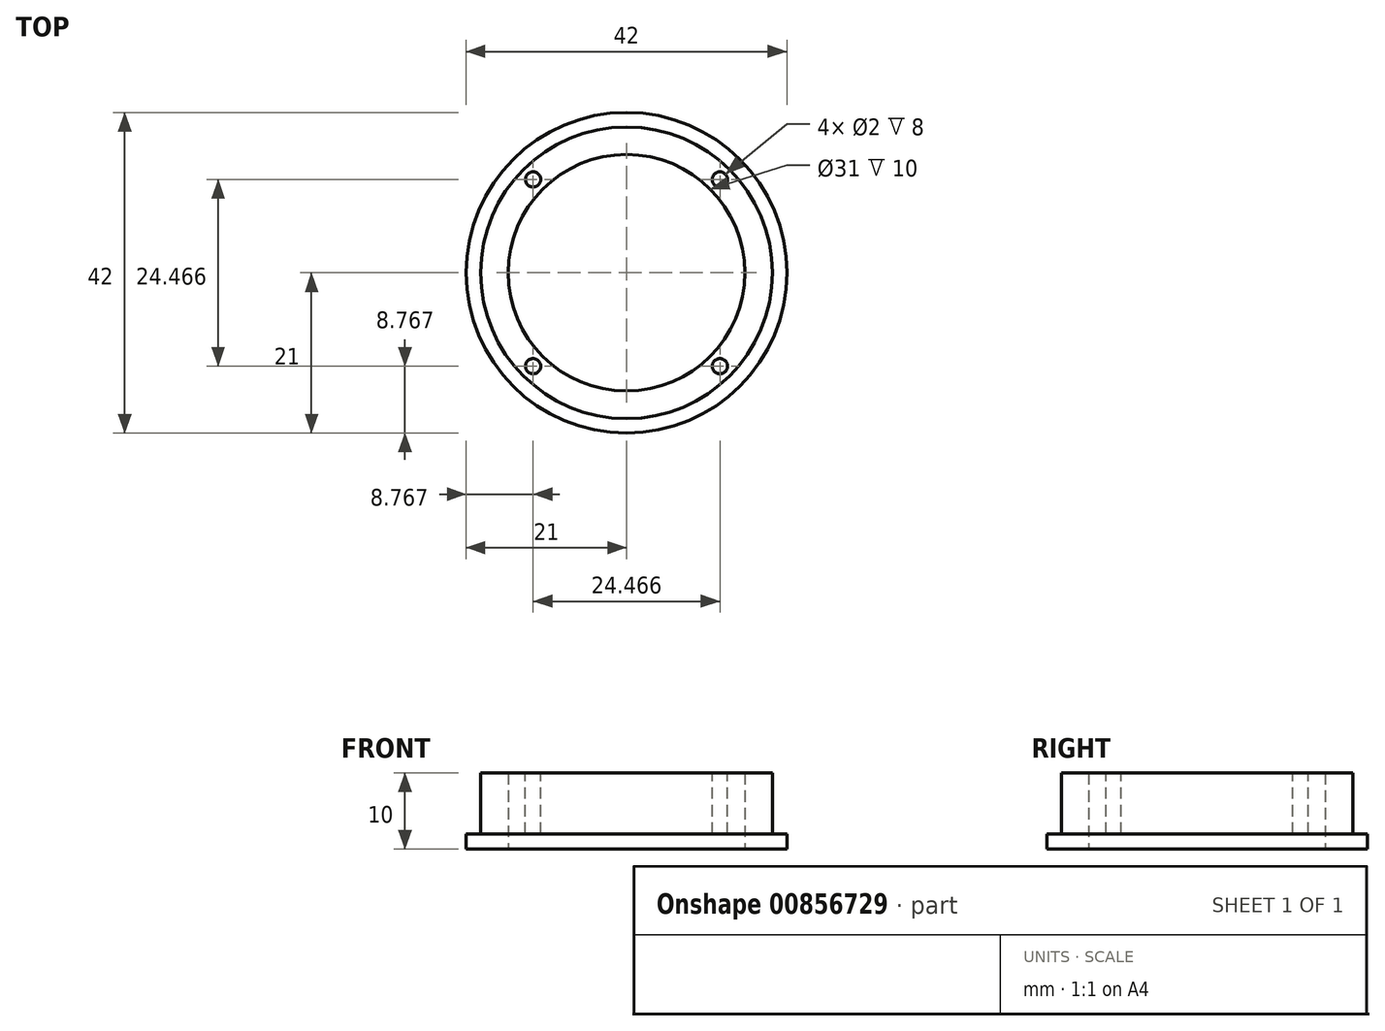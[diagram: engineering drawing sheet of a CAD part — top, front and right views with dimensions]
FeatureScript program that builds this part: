
annotation { "Feature Type Name" : "Feature", "Feature Type Description" : "" }
export const myFeature = defineFeature(function(context is Context, id is Id, definition is map)
    precondition{}
    {
        {
            var Q0;
            Q0=qCreatedBy(makeId("Top.planeOp"),FACE);
            var sketch = newSketch(context, id + "F0", { "sketchPlane" : qUnion([Q0])});
            skCircle(sketch, "E0", {"center": v(0, 0) * mm, "radius": 21 * mm});
            skSolve(sketch);
        }
        {
            var Q0;
            Q0=makeQuery(id+"F0.imprint","IMPRINT",FACE,{"disambiguationData":[TD([[makeQuery(id+"F0.imprint","IMPRINT",EDGE,{"derivedFrom":sQuery(id+"F0.wireOp",EDGE,"E0")}),1.0]])]});
            extrude(context, id + "F1", {"entities" : qUnion([Q0]), "depth" : 2 * mm, "offsetDistance" : 25 * mm});
        }
        {
            var Q0;
            Q0=makeQuery(id+"F1.opExtrude","CAP_FACE",FACE,{"disambiguationData":[OSD([sQuery(id+"F0.wireOp",EDGE,"E0")])],"isStart":false});
            var sketch = newSketch(context, id + "F2", { "sketchPlane" : qUnion([Q0])});
            skCircle(sketch, "E1", {"center": v(0, 0) * mm, "radius": 19.1 * mm});
            skSolve(sketch);
        }
        {
            var Q0;
            Q0=makeQuery(id+"F2.imprint","IMPRINT",FACE,{"disambiguationData":[TD([[makeQuery(id+"F2.imprint","IMPRINT",EDGE,{"derivedFrom":sQuery(id+"F2.wireOp",EDGE,"E1")}),1.0]])]});
            extrude(context, id + "F3", {"entities" : qUnion([Q0]), "operationType" : NewBodyOperationType.ADD, "depth" : 8 * mm, "offsetDistance" : 25 * mm});
        }
        {
            var Q0;
            Q0=makeQuery(id+"F1.opExtrude","CAP_FACE",FACE,{"disambiguationData":[OSD([sQuery(id+"F0.wireOp",EDGE,"E0")])],"isStart":true});
            var sketch = newSketch(context, id + "F4", { "sketchPlane" : qUnion([Q0])});
            skCircle(sketch, "E2", {"center": v(0, 0) * mm, "radius": 15.5 * mm});
            skSolve(sketch);
        }
        {
            var Q0;
            Q0=makeQuery(id+"F4.imprint","IMPRINT",FACE,{"disambiguationData":[TD([[makeQuery(id+"F4.imprint","IMPRINT",EDGE,{"derivedFrom":sQuery(id+"F4.wireOp",EDGE,"E2")}),1.0]])]});
            extrude(context, id + "F5", {"entities" : qUnion([Q0]), "operationType" : NewBodyOperationType.REMOVE, "endBound" : BoundingType.UP_TO_NEXT, "oppositeDirection" : true, "depth" : 25 * mm, "offsetDistance" : 25 * mm});
        }
        {
            var Q0;
            Q0=makeQuery(id+"F3.opExtrude","CAP_FACE",FACE,{"disambiguationData":[OSD([sQuery(id+"F2.wireOp",EDGE,"E1")])],"isStart":false});
            var sketch = newSketch(context, id + "F6", { "sketchPlane" : qUnion([Q0])});
            skLineSegment(sketch, "E3", {"start": v(0, 0) * mm, "end": v(-24.47, 24.47) * mm, "construction": true});
            skPoint(sketch, "E4.center", {"position": v(0, 0) * mm});
            skCircle(sketch, "E5", {"center": v(-12.23, 12.23) * mm, "radius": 1 * mm});
            skCircle(sketch, "E6.1.0", {"center": v(-12.23, -12.23) * mm, "radius": 1 * mm});
            skCircle(sketch, "E6.2.0", {"center": v(12.23, -12.23) * mm, "radius": 1 * mm});
            skCircle(sketch, "E6.3.0", {"center": v(12.23, 12.23) * mm, "radius": 1 * mm});
            skSolve(sketch);
        }
        {
            var Q0;
            Q0=makeQuery(id+"F6.imprint","IMPRINT",FACE,{"disambiguationData":[TD([[makeQuery(id+"F6.imprint","IMPRINT",EDGE,{"derivedFrom":sQuery(id+"F6.wireOp",EDGE,"E5")}),1.0]])]});
            var Q1;
            Q1=makeQuery(id+"F6.imprint","IMPRINT",FACE,{"disambiguationData":[TD([[makeQuery(id+"F6.imprint","IMPRINT",EDGE,{"derivedFrom":sQuery(id+"F6.wireOp",EDGE,"E6.3.0")}),1.0]])]});
            var Q2;
            Q2=makeQuery(id+"F6.imprint","IMPRINT",FACE,{"disambiguationData":[TD([[makeQuery(id+"F6.imprint","IMPRINT",EDGE,{"derivedFrom":sQuery(id+"F6.wireOp",EDGE,"E6.1.0")}),1.0]])]});
            var Q3;
            Q3=makeQuery(id+"F6.imprint","IMPRINT",FACE,{"disambiguationData":[TD([[makeQuery(id+"F6.imprint","IMPRINT",EDGE,{"derivedFrom":sQuery(id+"F6.wireOp",EDGE,"E6.2.0")}),1.0]])]});
            extrude(context, id + "F7", {"entities" : qUnion([Q0, Q1, Q2, Q3]), "operationType" : NewBodyOperationType.REMOVE, "oppositeDirection" : true, "depth" : 8 * mm, "offsetDistance" : 25 * mm});
        }
    });
